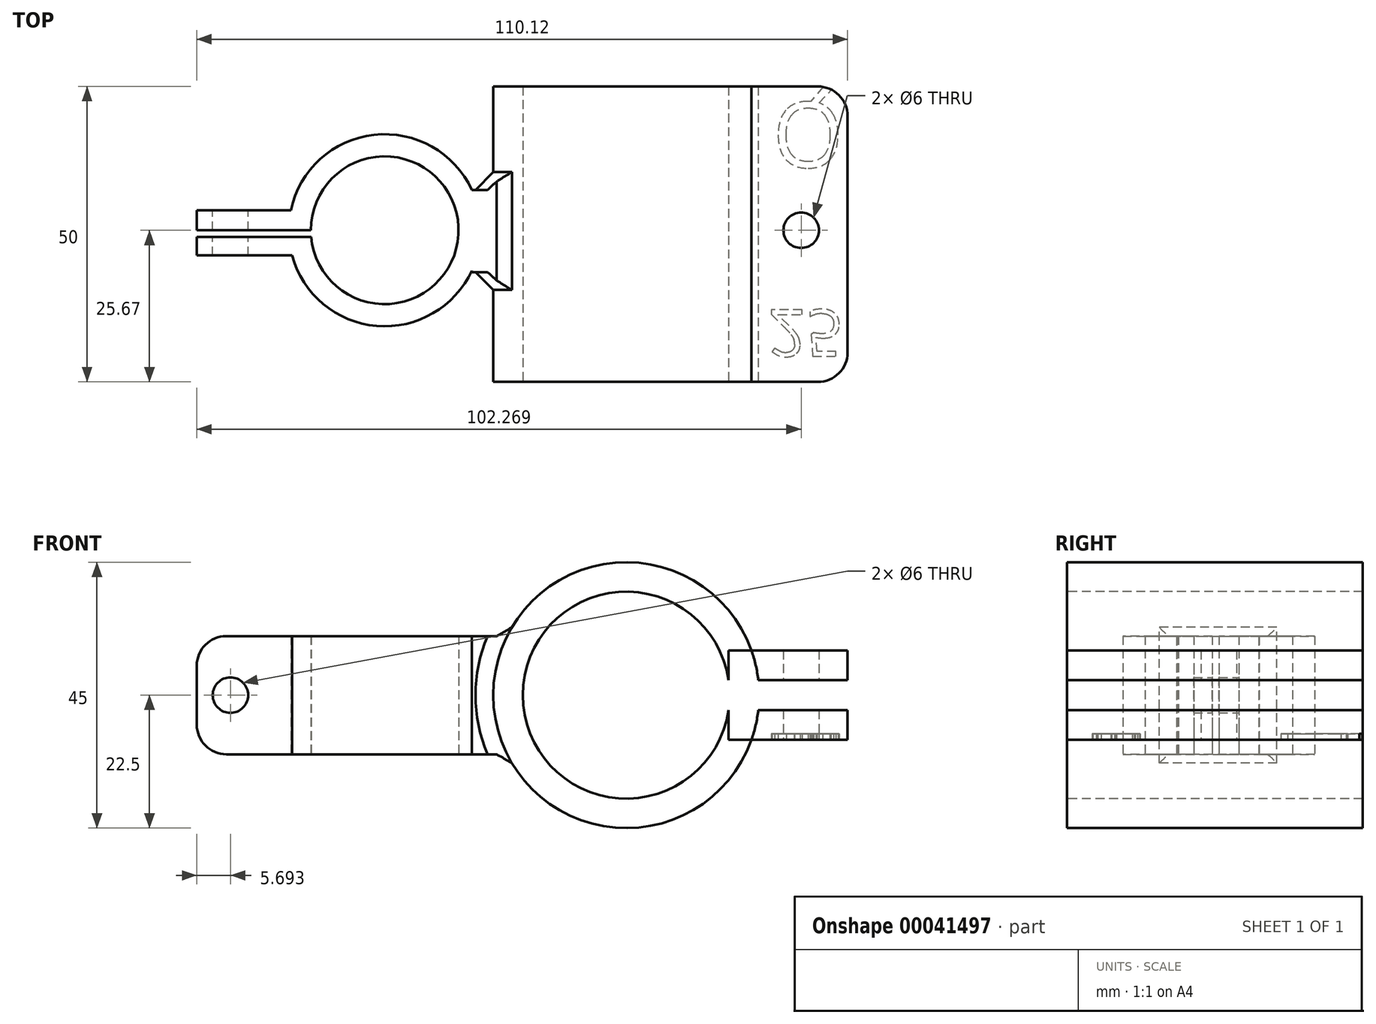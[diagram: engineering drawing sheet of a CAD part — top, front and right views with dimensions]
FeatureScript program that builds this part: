
annotation { "Feature Type Name" : "Feature", "Feature Type Description" : "" }
export const myFeature = defineFeature(function(context is Context, id is Id, definition is map)
    precondition{}
    {
        {
            var Q0;
            Q0=qCreatedBy(makeId("Top.planeOp"),FACE);
            var sketch = newSketch(context, id + "F0", { "sketchPlane" : qUnion([Q0])});
            skArc(sketch, "E0", {"start": v(-12.45, -1.1) * mm, "mid": v(12.49, 0.55) * mm, "end": v(-12.5, 0) * mm});
            skLineSegment(sketch, "E1.bottom", {"start": v(-12.5, 0) * mm, "end": v(-31.8, 0) * mm});
            skLineSegment(sketch, "E1.top", {"start": v(-15.9, 3.4) * mm, "end": v(-31.8, 3.4) * mm});
            skLineSegment(sketch, "E1.right", {"start": v(-31.8, 0) * mm, "end": v(-31.8, 3.4) * mm});
            skLineSegment(sketch, "E2.bottom", {"start": v(-12.45, -1.1) * mm, "end": v(-31.8, -1.1) * mm});
            skLineSegment(sketch, "E2.top", {"start": v(-15.68, -4.25) * mm, "end": v(-31.8, -4.25) * mm});
            skLineSegment(sketch, "E2.right", {"start": v(-31.8, -1.1) * mm, "end": v(-31.8, -4.25) * mm});
            skArc(sketch, "E3.trimOffspring", {"start": v(-15.68, -4.25) * mm, "mid": v(-1.37, -16.2) * mm, "end": v(14.74, -6.83) * mm});
            skLineSegment(sketch, "E4.bottom", {"start": v(14.74, 6.83) * mm, "end": v(26.47, 6.83) * mm});
            skLineSegment(sketch, "E4.top", {"start": v(14.74, -7.08) * mm, "end": v(26.47, -7.08) * mm});
            skLineSegment(sketch, "E4.left", {"start": v(14.74, -6.83) * mm, "end": v(14.74, -7.08) * mm});
            skLineSegment(sketch, "E4.right", {"start": v(26.47, 6.83) * mm, "end": v(26.47, -7.08) * mm});
            skArc(sketch, "E5.trimOffspring", {"start": v(14.74, 6.83) * mm, "mid": v(-1.8, 16.15) * mm, "end": v(-15.9, 3.4) * mm});
            skSolve(sketch);
        }
        {
            var Q0;
            Q0=makeQuery(id+"F0.imprint","IMPRINT",FACE,{"disambiguationData":[TD([[makeQuery(id+"F0.imprint","IMPRINT",EDGE,{"derivedFrom":sQuery(id+"F0.wireOp",EDGE,"E0")}),-1.0]])]});
            extrude(context, id + "F1", {"entities" : qUnion([Q0]), "depth" : 20 * mm});
        }
        {
            var Q0;
            Q0=makeQuery(id+"F1.opExtrude","SWEPT_FACE",FACE,{"disambiguationData":[OSD([sQuery(id+"F0.wireOp",EDGE,"E1.top")])]});
            var sketch = newSketch(context, id + "F2", { "sketchPlane" : qUnion([Q0])});
            skCircle(sketch, "E6", {"center": v(26.1, 10) * mm, "radius": 3 * mm});
            skPoint(sketch, "E6.centerSnap0", {"position": v(31.8, 10) * mm});
            skSolve(sketch);
        }
        {
            var Q0;
            Q0=makeQuery(id+"F2.imprint","IMPRINT",FACE,{"disambiguationData":[TD([[makeQuery(id+"F2.imprint","IMPRINT",EDGE,{"derivedFrom":sQuery(id+"F2.wireOp",EDGE,"E6")}),1.0]])]});
            extrude(context, id + "F3", {"entities" : qUnion([Q0]), "operationType" : NewBodyOperationType.REMOVE, "endBound" : BoundingType.THROUGH_ALL, "oppositeDirection" : true, "depth" : 25 * mm});
        }
        {
            var Q0;
            Q0=makeQuery(id+"F1.opExtrude","SWEPT_FACE",FACE,{"disambiguationData":[OSD([sQuery(id+"F0.wireOp",EDGE,"E4.bottom")])]});
            var sketch = newSketch(context, id + "F4", { "sketchPlane" : qUnion([Q0])});
            skCircle(sketch, "E7", {"center": v(-40.87, 10) * mm, "radius": 22.5 * mm});
            skPoint(sketch, "E7.centerSnap0", {"position": v(-26.47, 10) * mm});
            skCircle(sketch, "E8", {"center": v(-40.87, 10) * mm, "radius": 17.5 * mm});
            skSolve(sketch);
        }
        {
            var Q0;
            {var subQ0=sQuery(id+"F0.wireOp",EDGE,"E4.bottom");var subQ1=makeQuery(id+"F1.opExtrude","CAP_EDGE",EDGE,{"disambiguationData":[OSD([subQ0])],"isStart":true});var subQ9=sQuery(id+"F4.wireOp",EDGE,"E7");var subQ10=makeQuery(id+"F4.imprint","INTERSECT",VERTEX,{"derivedFrom":[subQ1,subQ9]});Q0=makeQuery(id+"F4.imprint","IMPRINT",FACE,{"disambiguationData":[TD([[makeQuery(id+"F4.imprint","IMPRINT",EDGE,{"disambiguationData":[TD([[subQ10,1.0]])],"derivedFrom":subQ9}),1.0]])]});}
            var Q1;
            {var subQ0=sQuery(id+"F0.wireOp",EDGE,"E4.bottom");var subQ7=makeQuery(id+"F1.opExtrude","CAP_EDGE",EDGE,{"disambiguationData":[OSD([subQ0])],"isStart":true});var subQ9=sQuery(id+"F4.wireOp",EDGE,"E7");var subQ10=makeQuery(id+"F4.imprint","INTERSECT",VERTEX,{"derivedFrom":[subQ7,subQ9]});Q1=makeQuery(id+"F4.imprint","IMPRINT",FACE,{"disambiguationData":[TD([[makeQuery(id+"F4.imprint","IMPRINT",EDGE,{"disambiguationData":[TD([[subQ10,-1.0]])],"derivedFrom":subQ9}),1.0]])]});}
            var Q2;
            Q2=sQuery(id+"F4.wireOp",EDGE,"E7");
            extrude(context, id + "F5", {"entities" : qUnion([Q0, Q1]), "operationType" : NewBodyOperationType.ADD, "surfaceEntities" : qUnion([Q2]), "depth" : 35 * mm, "symmetric" : true});
        }
        {
            var Q0;
            Q0=makeQuery(id+"F5.boolean.opBoolean","SPLIT",FACE,{"disambiguationData":[TD([makeQuery(id+"F1.opExtrude","SWEPT_FACE",FACE,{"disambiguationData":[OSD([sQuery(id+"F0.wireOp",EDGE,"E4.right")])]})])],"derivedFrom":makeQuery(id+"F1.opExtrude","SWEPT_FACE",FACE,{"disambiguationData":[OSD([sQuery(id+"F0.wireOp",EDGE,"E4.top")])]})});
            extrude(context, id + "F6", {"entities" : qUnion([Q0]), "operationType" : NewBodyOperationType.REMOVE, "oppositeDirection" : true, "depth" : 25 * mm});
        }
        {
            var Q0;
            Q0=makeQuery(id+"F5.opExtrude","CAP_FACE",FACE,{"disambiguationData":[OSD([sQuery(id+"F4.wireOp",EDGE,"E7"),sQuery(id+"F4.wireOp",EDGE,"E8")])],"isStart":true});
            var sketch = newSketch(context, id + "F7", { "sketchPlane" : qUnion([Q0])});
            skLineSegment(sketch, "E9.bottom", {"start": v(58.18, 7.44) * mm, "end": v(78.32, 7.44) * mm});
            skLineSegment(sketch, "E9.top", {"start": v(58.18, 2.44) * mm, "end": v(78.32, 2.44) * mm});
            skLineSegment(sketch, "E9.left", {"start": v(58.18, 7.44) * mm, "end": v(58.18, 2.44) * mm});
            skLineSegment(sketch, "E9.right", {"start": v(78.32, 7.44) * mm, "end": v(78.32, 2.44) * mm});
            skPoint(sketch, "E10.oppositeSnap0", {"position": v(78.32, 4.94) * mm});
            skLineSegment(sketch, "E10.bottom", {"start": v(58.18, 12.56) * mm, "end": v(78.32, 12.56) * mm});
            skLineSegment(sketch, "E10.top", {"start": v(58.18, 17.56) * mm, "end": v(78.32, 17.56) * mm});
            skLineSegment(sketch, "E10.left", {"start": v(58.18, 12.56) * mm, "end": v(58.18, 17.56) * mm});
            skLineSegment(sketch, "E10.right", {"start": v(78.32, 12.56) * mm, "end": v(78.32, 17.56) * mm});
            skLineSegment(sketch, "E11.bottom", {"start": v(65.4, 7.44) * mm, "end": v(55.2, 7.44) * mm});
            skLineSegment(sketch, "E11.top", {"start": v(65.4, 12.56) * mm, "end": v(55.2, 12.56) * mm});
            skLineSegment(sketch, "E11.left", {"start": v(65.4, 7.44) * mm, "end": v(65.4, 12.56) * mm});
            skLineSegment(sketch, "E11.right", {"start": v(55.2, 7.44) * mm, "end": v(55.2, 12.56) * mm});
            skSolve(sketch);
        }
        {
            var Q0;
            {var subQ0=sQuery(id+"F7.wireOp",EDGE,"E11.bottom");var subQ3=makeQuery(id+"F5.opExtrude","CAP_EDGE",EDGE,{"disambiguationData":[OSD([sQuery(id+"F4.wireOp",EDGE,"E7")])],"isStart":true});var subQ4=makeQuery(id+"F7.imprint","INTERSECT",VERTEX,{"derivedFrom":[subQ3,subQ0]});Q0=makeQuery(id+"F7.imprint","IMPRINT",FACE,{"disambiguationData":[TD([[makeQuery(id+"F7.imprint","IMPRINT",EDGE,{"disambiguationData":[TD([[subQ4,1.0]])],"derivedFrom":subQ3}),-1.0]])]});}
            var Q1;
            Q1=makeQuery(id+"F5.opExtrude","CAP_FACE",FACE,{"disambiguationData":[OSD([sQuery(id+"F4.wireOp",EDGE,"E7"),sQuery(id+"F4.wireOp",EDGE,"E8")])],"isStart":false});
            extrude(context, id + "F8", {"entities" : qUnion([Q0]), "operationType" : NewBodyOperationType.REMOVE, "endBound" : BoundingType.UP_TO_SURFACE, "oppositeDirection" : true, "endBoundEntityFace" : qUnion([Q1]), "depth" : 25 * mm});
        }
        {
            var Q0;
            {var subQ0=sQuery(id+"F7.wireOp",EDGE,"E9.right");Q0=makeQuery(id+"F7.imprint","IMPRINT",FACE,{"disambiguationData":[TD([[makeQuery(id+"F7.imprint","IMPRINT",EDGE,{"derivedFrom":subQ0}),-1.0]])]});}
            var Q1;
            {var subQ0=sQuery(id+"F7.wireOp",EDGE,"E10.right");Q1=makeQuery(id+"F7.imprint","IMPRINT",FACE,{"disambiguationData":[TD([[makeQuery(id+"F7.imprint","IMPRINT",EDGE,{"derivedFrom":subQ0}),1.0]])]});}
            var Q2;
            Q2=makeQuery(id+"F5.opExtrude","CAP_FACE",FACE,{"disambiguationData":[OSD([sQuery(id+"F4.wireOp",EDGE,"E7"),sQuery(id+"F4.wireOp",EDGE,"E8")])],"isStart":false});
            extrude(context, id + "F9", {"entities" : qUnion([Q0, Q1]), "operationType" : NewBodyOperationType.ADD, "endBound" : BoundingType.UP_TO_SURFACE, "oppositeDirection" : true, "endBoundEntityFace" : qUnion([Q2]), "depth" : 25 * mm});
        }
        {
            var Q0;
            {var subQ0=sQuery(id+"F4.wireOp",EDGE,"E7");Q0=makeQuery(id+"F9.boolean.opBoolean","MERGE",FACE,{"derivedFrom":[makeQuery(id+"F5.opExtrude","CAP_FACE",FACE,{"disambiguationData":[OSD([subQ0,sQuery(id+"F4.wireOp",EDGE,"E8")])],"isStart":true}),makeQuery(id+"F9.opExtrude","CAP_FACE",FACE,{"disambiguationData":[OSD([subQ0,sQuery(id+"F7.wireOp",EDGE,"E9.bottom"),sQuery(id+"F7.wireOp",EDGE,"E9.top"),sQuery(id+"F7.wireOp",EDGE,"E9.right"),sQuery(id+"F7.wireOp",EDGE,"E11.bottom")])],"isStart":true}),makeQuery(id+"F9.opExtrude","CAP_FACE",FACE,{"disambiguationData":[OSD([subQ0,sQuery(id+"F7.wireOp",EDGE,"E10.bottom"),sQuery(id+"F7.wireOp",EDGE,"E10.top"),sQuery(id+"F7.wireOp",EDGE,"E10.right"),sQuery(id+"F7.wireOp",EDGE,"E11.top")])],"isStart":true})]});}
            extrude(context, id + "F10", {"entities" : qUnion([Q0]), "operationType" : NewBodyOperationType.ADD, "depth" : 15 * mm});
        }
        {
            var Q0;
            Q0=makeQuery(id+"F5.boolean.opBoolean","INTERSECT",EDGE,{"derivedFrom":[makeQuery(id+"F1.opExtrude","CAP_FACE",FACE,{"disambiguationData":[OSD([sQuery(id+"F0.wireOp",EDGE,"E0"),sQuery(id+"F0.wireOp",EDGE,"E1.bottom"),sQuery(id+"F0.wireOp",EDGE,"E1.top"),sQuery(id+"F0.wireOp",EDGE,"E1.right"),sQuery(id+"F0.wireOp",EDGE,"E2.bottom"),sQuery(id+"F0.wireOp",EDGE,"E2.top"),sQuery(id+"F0.wireOp",EDGE,"E2.right"),sQuery(id+"F0.wireOp",EDGE,"E3.trimOffspring"),sQuery(id+"F0.wireOp",EDGE,"E4.bottom"),sQuery(id+"F0.wireOp",EDGE,"E4.top"),sQuery(id+"F0.wireOp",EDGE,"E4.left"),sQuery(id+"F0.wireOp",EDGE,"E4.right"),sQuery(id+"F0.wireOp",EDGE,"E5.trimOffspring")])],"isStart":true}),makeQuery(id+"F5.opExtrude","SWEPT_FACE",FACE,{"disambiguationData":[OSD([sQuery(id+"F4.wireOp",EDGE,"E7")])]})]});
            var Q1;
            Q1=makeQuery(id+"F5.boolean.opBoolean","INTERSECT",EDGE,{"derivedFrom":[makeQuery(id+"F1.opExtrude","CAP_FACE",FACE,{"disambiguationData":[OSD([sQuery(id+"F0.wireOp",EDGE,"E0"),sQuery(id+"F0.wireOp",EDGE,"E1.bottom"),sQuery(id+"F0.wireOp",EDGE,"E1.top"),sQuery(id+"F0.wireOp",EDGE,"E1.right"),sQuery(id+"F0.wireOp",EDGE,"E2.bottom"),sQuery(id+"F0.wireOp",EDGE,"E2.top"),sQuery(id+"F0.wireOp",EDGE,"E2.right"),sQuery(id+"F0.wireOp",EDGE,"E3.trimOffspring"),sQuery(id+"F0.wireOp",EDGE,"E4.bottom"),sQuery(id+"F0.wireOp",EDGE,"E4.top"),sQuery(id+"F0.wireOp",EDGE,"E4.left"),sQuery(id+"F0.wireOp",EDGE,"E4.right"),sQuery(id+"F0.wireOp",EDGE,"E5.trimOffspring")])],"isStart":false}),makeQuery(id+"F5.opExtrude","SWEPT_FACE",FACE,{"disambiguationData":[OSD([sQuery(id+"F4.wireOp",EDGE,"E7")])]})]});
            var Q2;
            Q2=makeQuery(id+"F5.boolean.opBoolean","INTERSECT",EDGE,{"derivedFrom":[makeQuery(id+"F1.opExtrude","SWEPT_FACE",FACE,{"disambiguationData":[OSD([sQuery(id+"F0.wireOp",EDGE,"E4.bottom")])]}),makeQuery(id+"F5.opExtrude","SWEPT_FACE",FACE,{"disambiguationData":[OSD([sQuery(id+"F4.wireOp",EDGE,"E7")])]})]});
            var Q3;
            Q3=makeQuery(id+"F5.boolean.opBoolean","INTERSECT",EDGE,{"derivedFrom":[makeQuery(id+"F1.opExtrude","SWEPT_FACE",FACE,{"disambiguationData":[OSD([sQuery(id+"F0.wireOp",EDGE,"E4.top")])]}),makeQuery(id+"F5.opExtrude","SWEPT_FACE",FACE,{"disambiguationData":[OSD([sQuery(id+"F4.wireOp",EDGE,"E7")])]})]});
            chamfer(context, id + "F11", {"entities" : qUnion([Q0, Q1, Q2, Q3]), "width" : 3 * mm});
        }
        {
            var Q0;
            {var subQ0=sQuery(id+"F7.wireOp",EDGE,"E9.top");Q0=makeQuery(id+"F10.boolean.opBoolean","MERGE",FACE,{"derivedFrom":[makeQuery(id+"F9.opExtrude","SWEPT_FACE",FACE,{"disambiguationData":[OSD([subQ0])]}),makeQuery(id+"F10.opExtrude","SWEPT_FACE",FACE,{"disambiguationData":[OSD([subQ0])]})]});}
            var sketch = newSketch(context, id + "F12", { "sketchPlane" : qUnion([Q0])});
            skCircle(sketch, "E12", {"center": v(70.47, 0) * mm, "radius": 3 * mm});
            skPoint(sketch, "E12.centerSnap0", {"position": v(78.32, 0) * mm});
            skSolve(sketch);
        }
        {
            var Q0;
            Q0=qSketchRegion(id+"F12",true);
            extrude(context, id + "F13", {"entities" : qUnion([Q0]), "operationType" : NewBodyOperationType.REMOVE, "oppositeDirection" : true, "depth" : 25 * mm});
        }
        {
            var Q0;
            Q0=makeQuery(id+"F1.opExtrude","CAP_EDGE",EDGE,{"disambiguationData":[OSD([sQuery(id+"F0.wireOp",EDGE,"E2.right")])],"isStart":true});
            var Q1;
            Q1=makeQuery(id+"F1.opExtrude","CAP_EDGE",EDGE,{"disambiguationData":[OSD([sQuery(id+"F0.wireOp",EDGE,"E1.right")])],"isStart":true});
            var Q2;
            Q2=makeQuery(id+"F1.opExtrude","CAP_EDGE",EDGE,{"disambiguationData":[OSD([sQuery(id+"F0.wireOp",EDGE,"E2.right")])],"isStart":false});
            var Q3;
            Q3=makeQuery(id+"F1.opExtrude","CAP_EDGE",EDGE,{"disambiguationData":[OSD([sQuery(id+"F0.wireOp",EDGE,"E1.right")])],"isStart":false});
            var Q4;
            Q4=makeQuery(id+"F9.opExtrude","CAP_EDGE",EDGE,{"disambiguationData":[OSD([sQuery(id+"F7.wireOp",EDGE,"E9.right")])],"isStart":true});
            var Q5;
            Q5=makeQuery(id+"F9.opExtrude","CAP_EDGE",EDGE,{"disambiguationData":[OSD([sQuery(id+"F7.wireOp",EDGE,"E10.right")])],"isStart":true});
            var Q6;
            Q6=makeQuery(id+"F9.opExtrude","CAP_EDGE",EDGE,{"disambiguationData":[OSD([sQuery(id+"F7.wireOp",EDGE,"E10.right")])],"isStart":false});
            var Q7;
            Q7=makeQuery(id+"F9.opExtrude","CAP_EDGE",EDGE,{"disambiguationData":[OSD([sQuery(id+"F7.wireOp",EDGE,"E9.right")])],"isStart":false});
            var Q8;
            Q8=makeQuery(id+"F10.opExtrude","CAP_EDGE",EDGE,{"disambiguationData":[OSD([sQuery(id+"F7.wireOp",EDGE,"E9.right")])],"isStart":false});
            var Q9;
            Q9=makeQuery(id+"F10.opExtrude","CAP_EDGE",EDGE,{"disambiguationData":[OSD([sQuery(id+"F7.wireOp",EDGE,"E10.right")])],"isStart":false});
            fillet(context, id + "F14", {"entities" : qUnion([Q0, Q1, Q2, Q3, Q4, Q5, Q6, Q7, Q8, Q9]), "radius" : 5 * mm, "tangentPropagation" : true, "allowEdgeOverflow" : false});
        }
        {
            var Q0;
            {var subQ0=sQuery(id+"F7.wireOp",EDGE,"E9.top");Q0=makeQuery(id+"F10.boolean.opBoolean","MERGE",FACE,{"derivedFrom":[makeQuery(id+"F9.opExtrude","SWEPT_FACE",FACE,{"disambiguationData":[OSD([subQ0])]}),makeQuery(id+"F10.opExtrude","SWEPT_FACE",FACE,{"disambiguationData":[OSD([subQ0])]})]});}
            var sketch = newSketch(context, id + "F15", { "sketchPlane" : qUnion([Q0])});
            skText(sketch, "E13", { "text": "25", "fontName": "OpenSans-Regular.ttf"});
            skText(sketch, "E14", { "text": "Q", "fontName": "OpenSans-Regular.ttf"});
            const initialGuessF15  = {"E13": [0.0649, 0.01344, 1, 0, 0.00796], "E14": [0.06564, -0.02166, 1, 0, 0.0111]};
            skSetInitialGuess(sketch, initialGuessF15);
            skSolve(sketch);
        }
        {
            var Q0;
            Q0=qSketchRegion(id+"F15",true);
            extrude(context, id + "F16", {"entities" : qUnion([Q0]), "operationType" : NewBodyOperationType.REMOVE, "oppositeDirection" : true, "depth" : 1 * mm});
        }
    });
